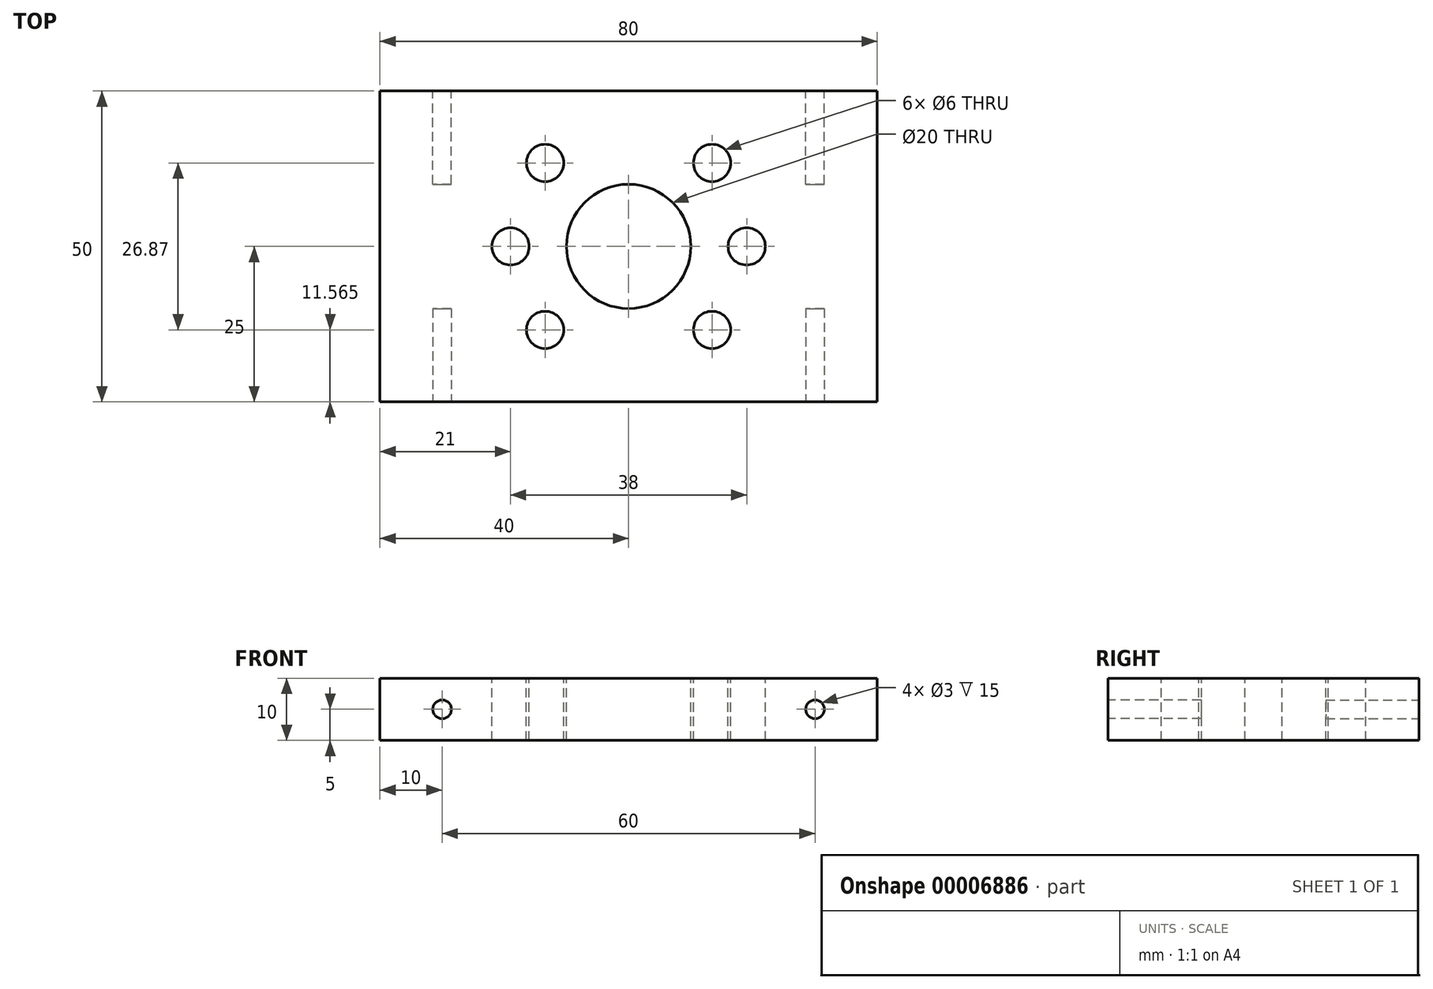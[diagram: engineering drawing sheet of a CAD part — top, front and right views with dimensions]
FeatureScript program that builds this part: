
annotation { "Feature Type Name" : "Feature", "Feature Type Description" : "" }
export const myFeature = defineFeature(function(context is Context, id is Id, definition is map)
    precondition{}
    {
        {
            var Q0;
            Q0=qCreatedBy(makeId("Top.planeOp"),FACE);
            var sketch = newSketch(context, id + "F0", { "sketchPlane" : qUnion([Q0])});
            skLineSegment(sketch, "E0.rect.bottom", {"start": v(40, -25) * mm, "end": v(-40, -25) * mm});
            skLineSegment(sketch, "E0.rect.top", {"start": v(40, 25) * mm, "end": v(-40, 25) * mm});
            skLineSegment(sketch, "E0.rect.left", {"start": v(40, -25) * mm, "end": v(40, 25) * mm});
            skLineSegment(sketch, "E0.rect.right", {"start": v(-40, -25) * mm, "end": v(-40, 25) * mm});
            skPoint(sketch, "E0.rect.middle", {"position": v(0, 0) * mm});
            skSolve(sketch);
        }
        {
            var Q0;
            {var subQ1=sQuery(id+"F0.wireOp",EDGE,"E0.rect.left");Q0=makeQuery(id+"F0.imprint","IMPRINT",FACE,{"disambiguationData":[TD([[makeQuery(id+"F0.imprint","IMPRINT",EDGE,{"derivedFrom":subQ1}),1.0]])]});}
            var Q1;
            {var subQ1=sQuery(id+"F0.wireOp",EDGE,"E0.rect.right");Q1=makeQuery(id+"F0.imprint","IMPRINT",FACE,{"disambiguationData":[TD([[makeQuery(id+"F0.imprint","IMPRINT",EDGE,{"derivedFrom":subQ1}),-1.0]])]});}
            extrude(context, id + "F1", {"entities" : qUnion([Q0, Q1]), "depth" : 10 * mm});
        }
        {
            var Q0;
            Q0=makeQuery(id+"F1.opExtrude","CAP_FACE",FACE,{"disambiguationData":[OSD([sQuery(id+"F0.wireOp",EDGE,"E0.rect.bottom"),sQuery(id+"F0.wireOp",EDGE,"E0.rect.top"),sQuery(id+"F0.wireOp",EDGE,"E0.rect.left"),sQuery(id+"F0.wireOp",EDGE,"E0.rect.right")])],"isStart":false});
            var sketch = newSketch(context, id + "F2", { "sketchPlane" : qUnion([Q0])});
            skLineSegment(sketch, "E1", {"start": v(0, 25) * mm, "end": v(0, -25) * mm, "construction": true});
            skLineSegment(sketch, "E2", {"start": v(20, 0) * mm, "end": v(-40, 0) * mm, "construction": true});
            skCircle(sketch, "E3", {"center": v(0, 0) * mm, "radius": 10 * mm});
            skCircle(sketch, "E4", {"center": v(0, 0) * mm, "radius": 19 * mm, "construction": true});
            skCircle(sketch, "E5", {"center": v(-19, 0) * mm, "radius": 3 * mm});
            skCircle(sketch, "E6", {"center": v(19, 0) * mm, "radius": 3 * mm});
            skLineSegment(sketch, "E7", {"start": v(0, 0) * mm, "end": v(-19.33, 19.33) * mm, "construction": true});
            skLineSegment(sketch, "E8", {"start": v(0, 0) * mm, "end": v(-18.3, -18.3) * mm, "construction": true});
            skLineSegment(sketch, "E9", {"start": v(0, 0) * mm, "end": v(16.8, 16.8) * mm, "construction": true});
            skLineSegment(sketch, "E10", {"start": v(0, 0) * mm, "end": v(17.78, -17.78) * mm, "construction": true});
            skCircle(sketch, "E11", {"center": v(-13.44, 13.44) * mm, "radius": 3 * mm});
            skCircle(sketch, "E12", {"center": v(-13.44, -13.44) * mm, "radius": 3 * mm});
            skCircle(sketch, "E13", {"center": v(13.44, -13.44) * mm, "radius": 3 * mm});
            skCircle(sketch, "E14", {"center": v(13.44, 13.44) * mm, "radius": 3 * mm});
            skSolve(sketch);
        }
        {
            var Q0;
            Q0=makeQuery(id+"F2.imprint","IMPRINT",FACE,{"disambiguationData":[TD([[makeQuery(id+"F2.imprint","IMPRINT",EDGE,{"derivedFrom":sQuery(id+"F2.wireOp",EDGE,"E3")}),1.0]])]});
            var Q1;
            Q1=makeQuery(id+"F2.imprint","IMPRINT",FACE,{"disambiguationData":[TD([[makeQuery(id+"F2.imprint","IMPRINT",EDGE,{"derivedFrom":sQuery(id+"F2.wireOp",EDGE,"E5")}),1.0]])]});
            var Q2;
            Q2=makeQuery(id+"F2.imprint","IMPRINT",FACE,{"disambiguationData":[TD([[makeQuery(id+"F2.imprint","IMPRINT",EDGE,{"derivedFrom":sQuery(id+"F2.wireOp",EDGE,"E6")}),1.0]])]});
            var Q3;
            Q3=makeQuery(id+"F2.imprint","IMPRINT",FACE,{"disambiguationData":[TD([[makeQuery(id+"F2.imprint","IMPRINT",EDGE,{"derivedFrom":sQuery(id+"F2.wireOp",EDGE,"E12")}),1.0]])]});
            var Q4;
            Q4=makeQuery(id+"F2.imprint","IMPRINT",FACE,{"disambiguationData":[TD([[makeQuery(id+"F2.imprint","IMPRINT",EDGE,{"derivedFrom":sQuery(id+"F2.wireOp",EDGE,"E13")}),1.0]])]});
            var Q5;
            Q5=makeQuery(id+"F2.imprint","IMPRINT",FACE,{"disambiguationData":[TD([[makeQuery(id+"F2.imprint","IMPRINT",EDGE,{"derivedFrom":sQuery(id+"F2.wireOp",EDGE,"E14")}),1.0]])]});
            var Q6;
            Q6=makeQuery(id+"F2.imprint","IMPRINT",FACE,{"disambiguationData":[TD([[makeQuery(id+"F2.imprint","IMPRINT",EDGE,{"derivedFrom":sQuery(id+"F2.wireOp",EDGE,"E11")}),1.0]])]});
            extrude(context, id + "F3", {"entities" : qUnion([Q0, Q1, Q2, Q3, Q4, Q5, Q6]), "operationType" : NewBodyOperationType.REMOVE, "oppositeDirection" : true, "depth" : 25 * mm});
        }
        {
            var Q0;
            Q0=makeQuery(id+"F1.opExtrude","SWEPT_FACE",FACE,{"disambiguationData":[OSD([sQuery(id+"F0.wireOp",EDGE,"E0.rect.bottom")])]});
            var sketch = newSketch(context, id + "F4", { "sketchPlane" : qUnion([Q0])});
            skCircle(sketch, "E15", {"center": v(-30, 5) * mm, "radius": 1.5 * mm});
            skCircle(sketch, "E16", {"center": v(30, 5) * mm, "radius": 1.5 * mm});
            skSolve(sketch);
        }
        {
            var Q0;
            Q0 = qSketchRegion(id + "F4", true);
            extrude(context, id + "F5", {"entities" : qUnion([Q0]), "operationType" : NewBodyOperationType.REMOVE, "oppositeDirection" : true, "depth" : 15 * mm});
        }
        {
            var Q0;
            Q0=makeQuery(id+"F1.opExtrude","SWEPT_FACE",FACE,{"disambiguationData":[OSD([sQuery(id+"F0.wireOp",EDGE,"E0.rect.top")])]});
            var sketch = newSketch(context, id + "F6", { "sketchPlane" : qUnion([Q0])});
            skCircle(sketch, "E17", {"center": v(-30, 5) * mm, "radius": 1.5 * mm});
            skCircle(sketch, "E18", {"center": v(30, 5) * mm, "radius": 1.5 * mm});
            skSolve(sketch);
        }
        {
            var Q0;
            Q0 = qSketchRegion(id + "F6", true);
            extrude(context, id + "F7", {"entities" : qUnion([Q0]), "operationType" : NewBodyOperationType.REMOVE, "oppositeDirection" : true, "depth" : 15 * mm});
        }
    });
